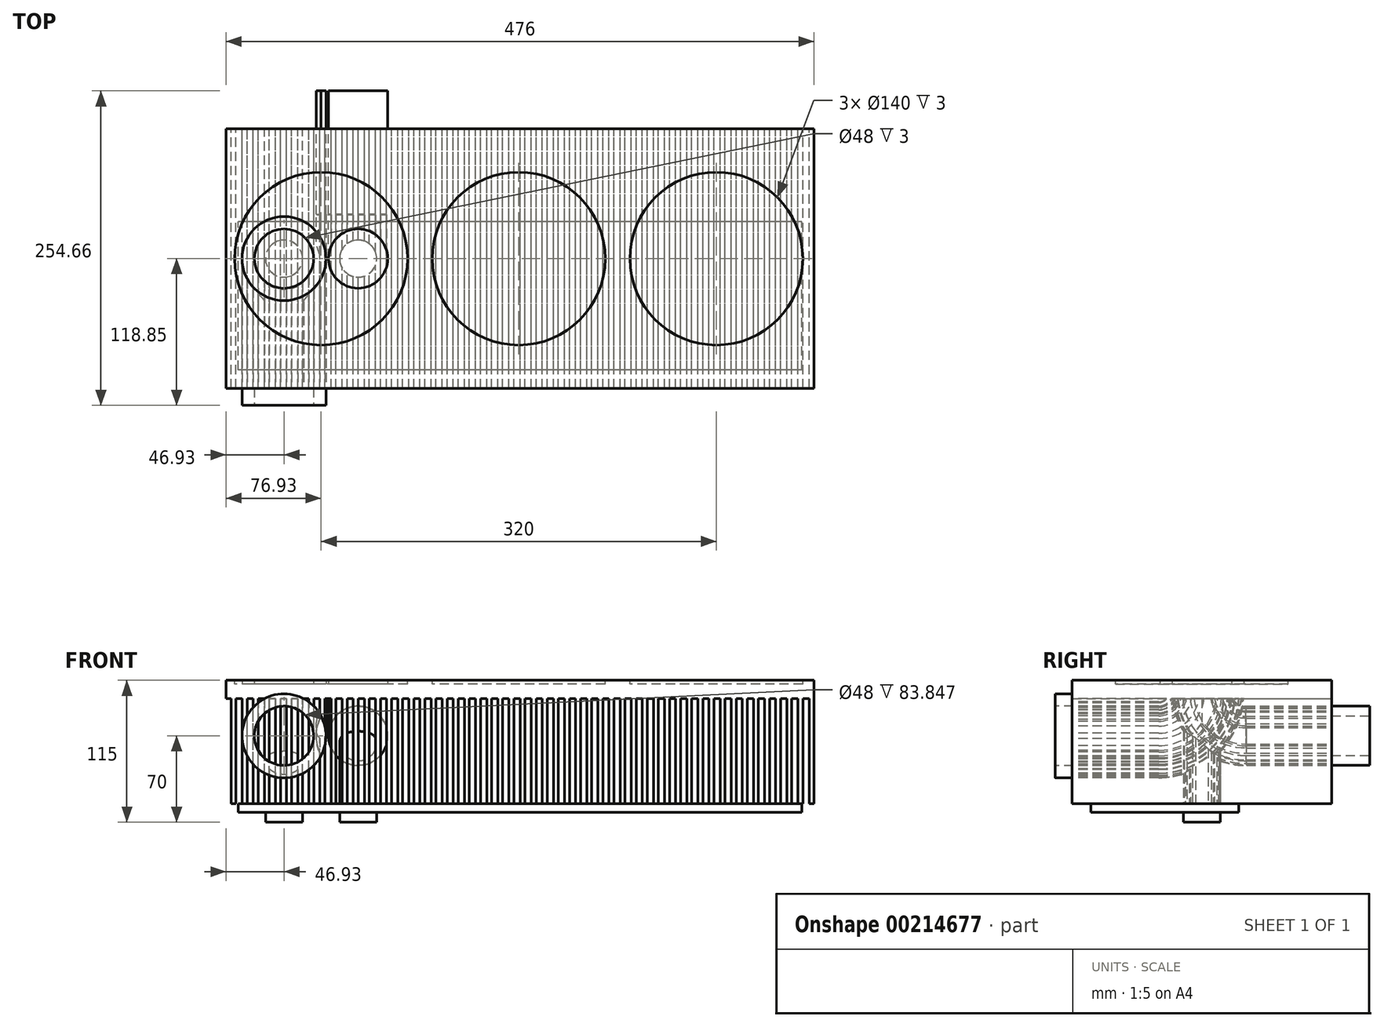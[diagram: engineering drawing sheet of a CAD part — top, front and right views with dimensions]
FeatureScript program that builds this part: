
annotation { "Feature Type Name" : "Feature", "Feature Type Description" : "" }
export const myFeature = defineFeature(function(context is Context, id is Id, definition is map)
    precondition{}
    {
        {
            var Q0;
            Q0=qCreatedBy(makeId("Top.planeOp"),FACE);
            var sketch = newSketch(context, id + "F0", { "sketchPlane" : qUnion([Q0])});
            skLineSegment(sketch, "E0.bottom", {"start": v(-236.93, 105) * mm, "end": v(239.07, 105) * mm});
            skLineSegment(sketch, "E0.top", {"start": v(-236.93, -105) * mm, "end": v(239.07, -105) * mm});
            skLineSegment(sketch, "E0.left", {"start": v(-236.93, 105) * mm, "end": v(-236.93, -105) * mm});
            skLineSegment(sketch, "E0.right", {"start": v(239.07, 105) * mm, "end": v(239.07, -105) * mm});
            skCircle(sketch, "E1", {"center": v(0, 0) * mm, "radius": 70 * mm});
            skCircle(sketch, "E2", {"center": v(160, 0) * mm, "radius": 70 * mm});
            skCircle(sketch, "E3", {"center": v(-160, 0) * mm, "radius": 70 * mm});
            skSolve(sketch);
        }
        {
            var Q0;
            Q0=makeQuery(id+"F0.imprint","IMPRINT",FACE,{"disambiguationData":[TD([[makeQuery(id+"F0.imprint","IMPRINT",EDGE,{"derivedFrom":sQuery(id+"F0.wireOp",EDGE,"E0.bottom")}),-1.0]])]});
            var Q1;
            Q1=makeQuery(id+"F0.imprint","IMPRINT",FACE,{"disambiguationData":[TD([[makeQuery(id+"F0.imprint","IMPRINT",EDGE,{"derivedFrom":sQuery(id+"F0.wireOp",EDGE,"E3")}),1.0]])]});
            var Q2;
            Q2=makeQuery(id+"F0.imprint","IMPRINT",FACE,{"disambiguationData":[TD([[makeQuery(id+"F0.imprint","IMPRINT",EDGE,{"derivedFrom":sQuery(id+"F0.wireOp",EDGE,"E1")}),1.0]])]});
            var Q3;
            Q3=makeQuery(id+"F0.imprint","IMPRINT",FACE,{"disambiguationData":[TD([[makeQuery(id+"F0.imprint","IMPRINT",EDGE,{"derivedFrom":sQuery(id+"F0.wireOp",EDGE,"E2")}),1.0]])]});
            extrude(context, id + "F1", {"entities" : qUnion([Q0, Q1, Q2, Q3]), "oppositeDirection" : true, "depth" : 15 * mm});
        }
        {
            var Q0;
            Q0=makeQuery(id+"F0.imprint","IMPRINT",FACE,{"disambiguationData":[TD([[makeQuery(id+"F0.imprint","IMPRINT",EDGE,{"derivedFrom":sQuery(id+"F0.wireOp",EDGE,"E3")}),1.0]])]});
            var Q1;
            Q1=makeQuery(id+"F0.imprint","IMPRINT",FACE,{"disambiguationData":[TD([[makeQuery(id+"F0.imprint","IMPRINT",EDGE,{"derivedFrom":sQuery(id+"F0.wireOp",EDGE,"E1")}),1.0]])]});
            var Q2;
            Q2=makeQuery(id+"F0.imprint","IMPRINT",FACE,{"disambiguationData":[TD([[makeQuery(id+"F0.imprint","IMPRINT",EDGE,{"derivedFrom":sQuery(id+"F0.wireOp",EDGE,"E2")}),1.0]])]});
            extrude(context, id + "F2", {"entities" : qUnion([Q0, Q1, Q2]), "operationType" : NewBodyOperationType.REMOVE, "oppositeDirection" : true, "depth" : 3 * mm});
        }
        {
            var Q0;
            Q0=makeQuery(id+"F0.imprint","IMPRINT",FACE,{"disambiguationData":[TD([[makeQuery(id+"F0.imprint","IMPRINT",EDGE,{"derivedFrom":sQuery(id+"F0.wireOp",EDGE,"E3")}),1.0]])]});
            var sketch = newSketch(context, id + "F3", { "sketchPlane" : qUnion([Q0])});
            skCircle(sketch, "E4", {"center": v(-190, 0) * mm, "radius": 24 * mm});
            skLineSegment(sketch, "E5", {"start": v(-160, 0) * mm, "end": v(-160, 31.63) * mm});
            skCircle(sketch, "E6.MirrorC", {"center": v(-130, 0) * mm, "radius": 24 * mm});
            skCircle(sketch, "E7", {"center": v(-190, 0) * mm, "radius": 34 * mm});
            skCircle(sketch, "E8.MirrorC", {"center": v(-130, 0) * mm, "radius": 34 * mm});
            skSolve(sketch);
        }
        {
            var Q0;
            Q0=makeQuery(id+"F1.opExtrude","CAP_FACE",FACE,{"disambiguationData":[OSD([sQuery(id+"F0.wireOp",EDGE,"E0.bottom"),sQuery(id+"F0.wireOp",EDGE,"E0.top"),sQuery(id+"F0.wireOp",EDGE,"E0.left"),sQuery(id+"F0.wireOp",EDGE,"E0.right")])],"isStart":false});
            var sketch = newSketch(context, id + "F4", { "sketchPlane" : qUnion([Q0])});
            skLineSegment(sketch, "E9", {"start": v(-130, 0) * mm, "end": v(-130, -36.8) * mm});
            skSolve(sketch);
        }
        {
            var Q0;
            Q0=qCreatedBy(makeId("Right.planeOp"),FACE);
            cPlane(context, id + "F5", {"entities" : qUnion([Q0]), "cplaneType" : CPlaneType.OFFSET, "offset" : 130 * mm, "oppositeDirection" : true, "width" : 150 * mm, "height" : 150 * mm});
        }
        {
            var Q0;
            Q0=qCreatedBy(id+"F5.planeOp",FACE);
            var sketch = newSketch(context, id + "F6", { "sketchPlane" : qUnion([Q0])});
            skLineSegment(sketch, "E10", {"start": v(0, 0) * mm, "end": v(0, -10) * mm});
            skLineSegment(sketch, "E11", {"start": v(0, -10) * mm, "end": v(35, -10) * mm});
            skArc(sketch, "E12", {"start": v(0, -10) * mm, "mid": v(10.54, -35.03) * mm, "end": v(35.8, -45) * mm});
            skLineSegment(sketch, "E13", {"start": v(35.8, -45) * mm, "end": v(135.8, -45) * mm});
            skSolve(sketch);
        }
        {
            var Q0;
            Q0=qCreatedBy(id+"F5.planeOp",FACE);
            cPlane(context, id + "F7", {"entities" : qUnion([Q0]), "cplaneType" : CPlaneType.OFFSET, "offset" : 60 * mm, "oppositeDirection" : true, "width" : 150 * mm, "height" : 150 * mm});
        }
        {
            var Q0;
            Q0=qCreatedBy(id+"F7.planeOp",FACE);
            var sketch = newSketch(context, id + "F8", { "sketchPlane" : qUnion([Q0])});
            skLineSegment(sketch, "E14", {"start": v(0, 0) * mm, "end": v(0, -10) * mm});
            skLineSegment(sketch, "E15", {"start": v(0, -10) * mm, "end": v(-35, -10) * mm});
            skArc(sketch, "E16", {"start": v(-35, -45) * mm, "mid": v(-10.25, -34.75) * mm, "end": v(0, -10) * mm});
            skLineSegment(sketch, "E17", {"start": v(-35, -45) * mm, "end": v(-118.85, -45) * mm});
            skSolve(sketch);
        }
        {
            var Q0;
            {var subQ0=sQuery(id+"F3.wireOp",EDGE,"E8.MirrorC");var subQ1=sQuery(id+"F3.wireOp",EDGE,"E7");var subQ2=makeQuery(id+"F3.imprint","INTERSECT",VERTEX,{"disambiguationData":[OD(0.0)],"derivedFrom":[subQ1,subQ0]});Q0=makeQuery(id+"F3.imprint","IMPRINT",FACE,{"disambiguationData":[TD([[makeQuery(id+"F3.imprint","IMPRINT",EDGE,{"disambiguationData":[TD([[subQ2,-1.0]])],"derivedFrom":subQ1}),1.0]])]});}
            var Q1;
            Q1=makeQuery(id+"F3.imprint","IMPRINT",FACE,{"disambiguationData":[TD([[makeQuery(id+"F3.imprint","IMPRINT",EDGE,{"derivedFrom":sQuery(id+"F3.wireOp",EDGE,"E4")}),-1.0]])]});
            var Q2;
            Q2=sQuery(id+"F8.wireOp",EDGE,"E17");
            var Q3;
            Q3=sQuery(id+"F8.wireOp",EDGE,"E16");
            var Q4;
            Q4=sQuery(id+"F8.wireOp",EDGE,"E14");
            sweep(context, id + "F9", {"operationType" : NewBodyOperationType.ADD, "profiles" : qUnion([Q0, Q1]), "path" : qUnion([Q2, Q3, Q4])});
        }
        {
            var Q0;
            Q0=makeQuery(id+"F4.imprint","IMPRINT",FACE,{"disambiguationData":[TD([[makeQuery(id+"F4.imprint","IMPRINT",EDGE,{"derivedFrom":makeQuery(id+"F1.opExtrude","CAP_EDGE",EDGE,{"disambiguationData":[OSD([sQuery(id+"F0.wireOp",EDGE,"E0.bottom")])],"isStart":false})}),1.0]])]});
            var sketch = newSketch(context, id + "F10", { "sketchPlane" : qUnion([Q0])});
            skLineSegment(sketch, "E18.bottom", {"start": v(235.07, 105) * mm, "end": v(239.07, 105) * mm});
            skLineSegment(sketch, "E18.top", {"start": v(235.07, -105) * mm, "end": v(239.07, -105) * mm});
            skLineSegment(sketch, "E18.left", {"start": v(235.07, 105) * mm, "end": v(235.07, -105) * mm});
            skLineSegment(sketch, "E18.right", {"start": v(239.07, 105) * mm, "end": v(239.07, -105) * mm});
            skLineSegment(sketch, "E19.1.0.0", {"start": v(226.07, 105) * mm, "end": v(226.07, -105) * mm});
            skLineSegment(sketch, "E19.1.0.1", {"start": v(230.07, 105) * mm, "end": v(230.07, -105) * mm});
            skLineSegment(sketch, "E19.1.0.2", {"start": v(226.07, 105) * mm, "end": v(230.07, 105) * mm});
            skLineSegment(sketch, "E19.1.0.3", {"start": v(226.07, -105) * mm, "end": v(230.07, -105) * mm});
            skLineSegment(sketch, "E19.2.0.0", {"start": v(217.07, 105) * mm, "end": v(217.07, -105) * mm});
            skLineSegment(sketch, "E19.2.0.1", {"start": v(221.07, 105) * mm, "end": v(221.07, -105) * mm});
            skLineSegment(sketch, "E19.2.0.2", {"start": v(217.07, 105) * mm, "end": v(221.07, 105) * mm});
            skLineSegment(sketch, "E19.2.0.3", {"start": v(217.07, -105) * mm, "end": v(221.07, -105) * mm});
            skLineSegment(sketch, "E19.3.0.0", {"start": v(208.07, 105) * mm, "end": v(208.07, -105) * mm});
            skLineSegment(sketch, "E19.3.0.1", {"start": v(212.07, 105) * mm, "end": v(212.07, -105) * mm});
            skLineSegment(sketch, "E19.3.0.2", {"start": v(208.07, 105) * mm, "end": v(212.07, 105) * mm});
            skLineSegment(sketch, "E19.3.0.3", {"start": v(208.07, -105) * mm, "end": v(212.07, -105) * mm});
            skLineSegment(sketch, "E19.4.0.0", {"start": v(199.07, 105) * mm, "end": v(199.07, -105) * mm});
            skLineSegment(sketch, "E19.4.0.1", {"start": v(203.07, 105) * mm, "end": v(203.07, -105) * mm});
            skLineSegment(sketch, "E19.4.0.2", {"start": v(199.07, 105) * mm, "end": v(203.07, 105) * mm});
            skLineSegment(sketch, "E19.4.0.3", {"start": v(199.07, -105) * mm, "end": v(203.07, -105) * mm});
            skLineSegment(sketch, "E19.5.0.0", {"start": v(190.07, 105) * mm, "end": v(190.07, -105) * mm});
            skLineSegment(sketch, "E19.5.0.1", {"start": v(194.07, 105) * mm, "end": v(194.07, -105) * mm});
            skLineSegment(sketch, "E19.5.0.2", {"start": v(190.07, 105) * mm, "end": v(194.07, 105) * mm});
            skLineSegment(sketch, "E19.5.0.3", {"start": v(190.07, -105) * mm, "end": v(194.07, -105) * mm});
            skLineSegment(sketch, "E19.6.0.0", {"start": v(181.07, 105) * mm, "end": v(181.07, -105) * mm});
            skLineSegment(sketch, "E19.6.0.1", {"start": v(185.07, 105) * mm, "end": v(185.07, -105) * mm});
            skLineSegment(sketch, "E19.6.0.2", {"start": v(181.07, 105) * mm, "end": v(185.07, 105) * mm});
            skLineSegment(sketch, "E19.6.0.3", {"start": v(181.07, -105) * mm, "end": v(185.07, -105) * mm});
            skLineSegment(sketch, "E19.7.0.0", {"start": v(172.07, 105) * mm, "end": v(172.07, -105) * mm});
            skLineSegment(sketch, "E19.7.0.1", {"start": v(176.07, 105) * mm, "end": v(176.07, -105) * mm});
            skLineSegment(sketch, "E19.7.0.2", {"start": v(172.07, 105) * mm, "end": v(176.07, 105) * mm});
            skLineSegment(sketch, "E19.7.0.3", {"start": v(172.07, -105) * mm, "end": v(176.07, -105) * mm});
            skLineSegment(sketch, "E19.8.0.0", {"start": v(163.07, 105) * mm, "end": v(163.07, -105) * mm});
            skLineSegment(sketch, "E19.8.0.1", {"start": v(167.07, 105) * mm, "end": v(167.07, -105) * mm});
            skLineSegment(sketch, "E19.8.0.2", {"start": v(163.07, 105) * mm, "end": v(167.07, 105) * mm});
            skLineSegment(sketch, "E19.8.0.3", {"start": v(163.07, -105) * mm, "end": v(167.07, -105) * mm});
            skLineSegment(sketch, "E19.9.0.0", {"start": v(154.07, 105) * mm, "end": v(154.07, -105) * mm});
            skLineSegment(sketch, "E19.9.0.1", {"start": v(158.07, 105) * mm, "end": v(158.07, -105) * mm});
            skLineSegment(sketch, "E19.9.0.2", {"start": v(154.07, 105) * mm, "end": v(158.07, 105) * mm});
            skLineSegment(sketch, "E19.9.0.3", {"start": v(154.07, -105) * mm, "end": v(158.07, -105) * mm});
            skLineSegment(sketch, "E19.10.0.0", {"start": v(145.07, 105) * mm, "end": v(145.07, -105) * mm});
            skLineSegment(sketch, "E19.10.0.1", {"start": v(149.07, 105) * mm, "end": v(149.07, -105) * mm});
            skLineSegment(sketch, "E19.10.0.2", {"start": v(145.07, 105) * mm, "end": v(149.07, 105) * mm});
            skLineSegment(sketch, "E19.10.0.3", {"start": v(145.07, -105) * mm, "end": v(149.07, -105) * mm});
            skLineSegment(sketch, "E19.11.0.0", {"start": v(136.07, 105) * mm, "end": v(136.07, -105) * mm});
            skLineSegment(sketch, "E19.11.0.1", {"start": v(140.07, 105) * mm, "end": v(140.07, -105) * mm});
            skLineSegment(sketch, "E19.11.0.2", {"start": v(136.07, 105) * mm, "end": v(140.07, 105) * mm});
            skLineSegment(sketch, "E19.11.0.3", {"start": v(136.07, -105) * mm, "end": v(140.07, -105) * mm});
            skLineSegment(sketch, "E19.12.0.0", {"start": v(127.07, 105) * mm, "end": v(127.07, -105) * mm});
            skLineSegment(sketch, "E19.12.0.1", {"start": v(131.07, 105) * mm, "end": v(131.07, -105) * mm});
            skLineSegment(sketch, "E19.12.0.2", {"start": v(127.07, 105) * mm, "end": v(131.07, 105) * mm});
            skLineSegment(sketch, "E19.12.0.3", {"start": v(127.07, -105) * mm, "end": v(131.07, -105) * mm});
            skLineSegment(sketch, "E19.13.0.0", {"start": v(118.07, 105) * mm, "end": v(118.07, -105) * mm});
            skLineSegment(sketch, "E19.13.0.1", {"start": v(122.07, 105) * mm, "end": v(122.07, -105) * mm});
            skLineSegment(sketch, "E19.13.0.2", {"start": v(118.07, 105) * mm, "end": v(122.07, 105) * mm});
            skLineSegment(sketch, "E19.13.0.3", {"start": v(118.07, -105) * mm, "end": v(122.07, -105) * mm});
            skLineSegment(sketch, "E19.14.0.0", {"start": v(109.07, 105) * mm, "end": v(109.07, -105) * mm});
            skLineSegment(sketch, "E19.14.0.1", {"start": v(113.07, 105) * mm, "end": v(113.07, -105) * mm});
            skLineSegment(sketch, "E19.14.0.2", {"start": v(109.07, 105) * mm, "end": v(113.07, 105) * mm});
            skLineSegment(sketch, "E19.14.0.3", {"start": v(109.07, -105) * mm, "end": v(113.07, -105) * mm});
            skLineSegment(sketch, "E19.15.0.0", {"start": v(100.07, 105) * mm, "end": v(100.07, -105) * mm});
            skLineSegment(sketch, "E19.15.0.1", {"start": v(104.07, 105) * mm, "end": v(104.07, -105) * mm});
            skLineSegment(sketch, "E19.15.0.2", {"start": v(100.07, 105) * mm, "end": v(104.07, 105) * mm});
            skLineSegment(sketch, "E19.15.0.3", {"start": v(100.07, -105) * mm, "end": v(104.07, -105) * mm});
            skLineSegment(sketch, "E19.16.0.0", {"start": v(91.07, 105) * mm, "end": v(91.07, -105) * mm});
            skLineSegment(sketch, "E19.16.0.1", {"start": v(95.07, 105) * mm, "end": v(95.07, -105) * mm});
            skLineSegment(sketch, "E19.16.0.2", {"start": v(91.07, 105) * mm, "end": v(95.07, 105) * mm});
            skLineSegment(sketch, "E19.16.0.3", {"start": v(91.07, -105) * mm, "end": v(95.07, -105) * mm});
            skLineSegment(sketch, "E19.17.0.0", {"start": v(82.07, 105) * mm, "end": v(82.07, -105) * mm});
            skLineSegment(sketch, "E19.17.0.1", {"start": v(86.07, 105) * mm, "end": v(86.07, -105) * mm});
            skLineSegment(sketch, "E19.17.0.2", {"start": v(82.07, 105) * mm, "end": v(86.07, 105) * mm});
            skLineSegment(sketch, "E19.17.0.3", {"start": v(82.07, -105) * mm, "end": v(86.07, -105) * mm});
            skLineSegment(sketch, "E19.18.0.0", {"start": v(73.07, 105) * mm, "end": v(73.07, -105) * mm});
            skLineSegment(sketch, "E19.18.0.1", {"start": v(77.07, 105) * mm, "end": v(77.07, -105) * mm});
            skLineSegment(sketch, "E19.18.0.2", {"start": v(73.07, 105) * mm, "end": v(77.07, 105) * mm});
            skLineSegment(sketch, "E19.18.0.3", {"start": v(73.07, -105) * mm, "end": v(77.07, -105) * mm});
            skLineSegment(sketch, "E19.19.0.0", {"start": v(64.07, 105) * mm, "end": v(64.07, -105) * mm});
            skLineSegment(sketch, "E19.19.0.1", {"start": v(68.07, 105) * mm, "end": v(68.07, -105) * mm});
            skLineSegment(sketch, "E19.19.0.2", {"start": v(64.07, 105) * mm, "end": v(68.07, 105) * mm});
            skLineSegment(sketch, "E19.19.0.3", {"start": v(64.07, -105) * mm, "end": v(68.07, -105) * mm});
            skLineSegment(sketch, "E19.20.0.0", {"start": v(55.07, 105) * mm, "end": v(55.07, -105) * mm});
            skLineSegment(sketch, "E19.20.0.1", {"start": v(59.07, 105) * mm, "end": v(59.07, -105) * mm});
            skLineSegment(sketch, "E19.20.0.2", {"start": v(55.07, 105) * mm, "end": v(59.07, 105) * mm});
            skLineSegment(sketch, "E19.20.0.3", {"start": v(55.07, -105) * mm, "end": v(59.07, -105) * mm});
            skLineSegment(sketch, "E19.21.0.0", {"start": v(46.07, 105) * mm, "end": v(46.07, -105) * mm});
            skLineSegment(sketch, "E19.21.0.1", {"start": v(50.07, 105) * mm, "end": v(50.07, -105) * mm});
            skLineSegment(sketch, "E19.21.0.2", {"start": v(46.07, 105) * mm, "end": v(50.07, 105) * mm});
            skLineSegment(sketch, "E19.21.0.3", {"start": v(46.07, -105) * mm, "end": v(50.07, -105) * mm});
            skLineSegment(sketch, "E19.22.0.0", {"start": v(37.07, 105) * mm, "end": v(37.07, -105) * mm});
            skLineSegment(sketch, "E19.22.0.1", {"start": v(41.07, 105) * mm, "end": v(41.07, -105) * mm});
            skLineSegment(sketch, "E19.22.0.2", {"start": v(37.07, 105) * mm, "end": v(41.07, 105) * mm});
            skLineSegment(sketch, "E19.22.0.3", {"start": v(37.07, -105) * mm, "end": v(41.07, -105) * mm});
            skLineSegment(sketch, "E19.23.0.0", {"start": v(28.07, 105) * mm, "end": v(28.07, -105) * mm});
            skLineSegment(sketch, "E19.23.0.1", {"start": v(32.07, 105) * mm, "end": v(32.07, -105) * mm});
            skLineSegment(sketch, "E19.23.0.2", {"start": v(28.07, 105) * mm, "end": v(32.07, 105) * mm});
            skLineSegment(sketch, "E19.23.0.3", {"start": v(28.07, -105) * mm, "end": v(32.07, -105) * mm});
            skLineSegment(sketch, "E19.24.0.0", {"start": v(19.07, 105) * mm, "end": v(19.07, -105) * mm});
            skLineSegment(sketch, "E19.24.0.1", {"start": v(23.07, 105) * mm, "end": v(23.07, -105) * mm});
            skLineSegment(sketch, "E19.24.0.2", {"start": v(19.07, 105) * mm, "end": v(23.07, 105) * mm});
            skLineSegment(sketch, "E19.24.0.3", {"start": v(19.07, -105) * mm, "end": v(23.07, -105) * mm});
            skLineSegment(sketch, "E19.25.0.0", {"start": v(10.07, 105) * mm, "end": v(10.07, -105) * mm});
            skLineSegment(sketch, "E19.25.0.1", {"start": v(14.07, 105) * mm, "end": v(14.07, -105) * mm});
            skLineSegment(sketch, "E19.25.0.2", {"start": v(10.07, 105) * mm, "end": v(14.07, 105) * mm});
            skLineSegment(sketch, "E19.25.0.3", {"start": v(10.07, -105) * mm, "end": v(14.07, -105) * mm});
            skLineSegment(sketch, "E19.26.0.0", {"start": v(1.07, 105) * mm, "end": v(1.07, -105) * mm});
            skLineSegment(sketch, "E19.26.0.1", {"start": v(5.07, 105) * mm, "end": v(5.07, -105) * mm});
            skLineSegment(sketch, "E19.26.0.2", {"start": v(1.07, 105) * mm, "end": v(5.07, 105) * mm});
            skLineSegment(sketch, "E19.26.0.3", {"start": v(1.07, -105) * mm, "end": v(5.07, -105) * mm});
            skLineSegment(sketch, "E19.27.0.0", {"start": v(-7.93, 105) * mm, "end": v(-7.93, -105) * mm});
            skLineSegment(sketch, "E19.27.0.1", {"start": v(-3.93, 105) * mm, "end": v(-3.93, -105) * mm});
            skLineSegment(sketch, "E19.27.0.2", {"start": v(-7.93, 105) * mm, "end": v(-3.93, 105) * mm});
            skLineSegment(sketch, "E19.27.0.3", {"start": v(-7.93, -105) * mm, "end": v(-3.93, -105) * mm});
            skLineSegment(sketch, "E19.28.0.0", {"start": v(-16.93, 105) * mm, "end": v(-16.93, -105) * mm});
            skLineSegment(sketch, "E19.28.0.1", {"start": v(-12.93, 105) * mm, "end": v(-12.93, -105) * mm});
            skLineSegment(sketch, "E19.28.0.2", {"start": v(-16.93, 105) * mm, "end": v(-12.93, 105) * mm});
            skLineSegment(sketch, "E19.28.0.3", {"start": v(-16.93, -105) * mm, "end": v(-12.93, -105) * mm});
            skLineSegment(sketch, "E19.29.0.0", {"start": v(-25.93, 105) * mm, "end": v(-25.93, -105) * mm});
            skLineSegment(sketch, "E19.29.0.1", {"start": v(-21.93, 105) * mm, "end": v(-21.93, -105) * mm});
            skLineSegment(sketch, "E19.29.0.2", {"start": v(-25.93, 105) * mm, "end": v(-21.93, 105) * mm});
            skLineSegment(sketch, "E19.29.0.3", {"start": v(-25.93, -105) * mm, "end": v(-21.93, -105) * mm});
            skLineSegment(sketch, "E19.30.0.0", {"start": v(-34.93, 105) * mm, "end": v(-34.93, -105) * mm});
            skLineSegment(sketch, "E19.30.0.1", {"start": v(-30.93, 105) * mm, "end": v(-30.93, -105) * mm});
            skLineSegment(sketch, "E19.30.0.2", {"start": v(-34.93, 105) * mm, "end": v(-30.93, 105) * mm});
            skLineSegment(sketch, "E19.30.0.3", {"start": v(-34.93, -105) * mm, "end": v(-30.93, -105) * mm});
            skLineSegment(sketch, "E19.31.0.0", {"start": v(-43.93, 105) * mm, "end": v(-43.93, -105) * mm});
            skLineSegment(sketch, "E19.31.0.1", {"start": v(-39.93, 105) * mm, "end": v(-39.93, -105) * mm});
            skLineSegment(sketch, "E19.31.0.2", {"start": v(-43.93, 105) * mm, "end": v(-39.93, 105) * mm});
            skLineSegment(sketch, "E19.31.0.3", {"start": v(-43.93, -105) * mm, "end": v(-39.93, -105) * mm});
            skLineSegment(sketch, "E19.32.0.0", {"start": v(-52.93, 105) * mm, "end": v(-52.93, -105) * mm});
            skLineSegment(sketch, "E19.32.0.1", {"start": v(-48.93, 105) * mm, "end": v(-48.93, -105) * mm});
            skLineSegment(sketch, "E19.32.0.2", {"start": v(-52.93, 105) * mm, "end": v(-48.93, 105) * mm});
            skLineSegment(sketch, "E19.32.0.3", {"start": v(-52.93, -105) * mm, "end": v(-48.93, -105) * mm});
            skLineSegment(sketch, "E19.33.0.0", {"start": v(-61.93, 105) * mm, "end": v(-61.93, -105) * mm});
            skLineSegment(sketch, "E19.33.0.1", {"start": v(-57.93, 105) * mm, "end": v(-57.93, -105) * mm});
            skLineSegment(sketch, "E19.33.0.2", {"start": v(-61.93, 105) * mm, "end": v(-57.93, 105) * mm});
            skLineSegment(sketch, "E19.33.0.3", {"start": v(-61.93, -105) * mm, "end": v(-57.93, -105) * mm});
            skLineSegment(sketch, "E19.34.0.0", {"start": v(-70.93, 105) * mm, "end": v(-70.93, -105) * mm});
            skLineSegment(sketch, "E19.34.0.1", {"start": v(-66.93, 105) * mm, "end": v(-66.93, -105) * mm});
            skLineSegment(sketch, "E19.34.0.2", {"start": v(-70.93, 105) * mm, "end": v(-66.93, 105) * mm});
            skLineSegment(sketch, "E19.34.0.3", {"start": v(-70.93, -105) * mm, "end": v(-66.93, -105) * mm});
            skLineSegment(sketch, "E19.35.0.0", {"start": v(-79.93, 105) * mm, "end": v(-79.93, -105) * mm});
            skLineSegment(sketch, "E19.35.0.1", {"start": v(-75.93, 105) * mm, "end": v(-75.93, -105) * mm});
            skLineSegment(sketch, "E19.35.0.2", {"start": v(-79.93, 105) * mm, "end": v(-75.93, 105) * mm});
            skLineSegment(sketch, "E19.35.0.3", {"start": v(-79.93, -105) * mm, "end": v(-75.93, -105) * mm});
            skLineSegment(sketch, "E19.36.0.0", {"start": v(-88.93, 105) * mm, "end": v(-88.93, -105) * mm});
            skLineSegment(sketch, "E19.36.0.1", {"start": v(-84.93, 105) * mm, "end": v(-84.93, -105) * mm});
            skLineSegment(sketch, "E19.36.0.2", {"start": v(-88.93, 105) * mm, "end": v(-84.93, 105) * mm});
            skLineSegment(sketch, "E19.36.0.3", {"start": v(-88.93, -105) * mm, "end": v(-84.93, -105) * mm});
            skLineSegment(sketch, "E19.37.0.0", {"start": v(-97.93, 105) * mm, "end": v(-97.93, -105) * mm});
            skLineSegment(sketch, "E19.37.0.1", {"start": v(-93.93, 105) * mm, "end": v(-93.93, -105) * mm});
            skLineSegment(sketch, "E19.37.0.2", {"start": v(-97.93, 105) * mm, "end": v(-93.93, 105) * mm});
            skLineSegment(sketch, "E19.37.0.3", {"start": v(-97.93, -105) * mm, "end": v(-93.93, -105) * mm});
            skLineSegment(sketch, "E19.38.0.0", {"start": v(-106.93, 105) * mm, "end": v(-106.93, -105) * mm});
            skLineSegment(sketch, "E19.38.0.1", {"start": v(-102.93, 105) * mm, "end": v(-102.93, -105) * mm});
            skLineSegment(sketch, "E19.38.0.2", {"start": v(-106.93, 105) * mm, "end": v(-102.93, 105) * mm});
            skLineSegment(sketch, "E19.38.0.3", {"start": v(-106.93, -105) * mm, "end": v(-102.93, -105) * mm});
            skLineSegment(sketch, "E19.39.0.0", {"start": v(-115.93, 105) * mm, "end": v(-115.93, -105) * mm});
            skLineSegment(sketch, "E19.39.0.1", {"start": v(-111.93, 105) * mm, "end": v(-111.93, -105) * mm});
            skLineSegment(sketch, "E19.39.0.2", {"start": v(-115.93, 105) * mm, "end": v(-111.93, 105) * mm});
            skLineSegment(sketch, "E19.39.0.3", {"start": v(-115.93, -105) * mm, "end": v(-111.93, -105) * mm});
            skLineSegment(sketch, "E19.40.0.0", {"start": v(-124.93, 105) * mm, "end": v(-124.93, -105) * mm});
            skLineSegment(sketch, "E19.40.0.1", {"start": v(-120.93, 105) * mm, "end": v(-120.93, -105) * mm});
            skLineSegment(sketch, "E19.40.0.2", {"start": v(-124.93, 105) * mm, "end": v(-120.93, 105) * mm});
            skLineSegment(sketch, "E19.40.0.3", {"start": v(-124.93, -105) * mm, "end": v(-120.93, -105) * mm});
            skLineSegment(sketch, "E19.41.0.0", {"start": v(-133.93, 105) * mm, "end": v(-133.93, -105) * mm});
            skLineSegment(sketch, "E19.41.0.1", {"start": v(-129.93, 105) * mm, "end": v(-129.93, -105) * mm});
            skLineSegment(sketch, "E19.41.0.2", {"start": v(-133.93, 105) * mm, "end": v(-129.93, 105) * mm});
            skLineSegment(sketch, "E19.41.0.3", {"start": v(-133.93, -105) * mm, "end": v(-129.93, -105) * mm});
            skLineSegment(sketch, "E19.42.0.0", {"start": v(-142.93, 105) * mm, "end": v(-142.93, -105) * mm});
            skLineSegment(sketch, "E19.42.0.1", {"start": v(-138.93, 105) * mm, "end": v(-138.93, -105) * mm});
            skLineSegment(sketch, "E19.42.0.2", {"start": v(-142.93, 105) * mm, "end": v(-138.93, 105) * mm});
            skLineSegment(sketch, "E19.42.0.3", {"start": v(-142.93, -105) * mm, "end": v(-138.93, -105) * mm});
            skLineSegment(sketch, "E19.43.0.0", {"start": v(-151.93, 105) * mm, "end": v(-151.93, -105) * mm});
            skLineSegment(sketch, "E19.43.0.1", {"start": v(-147.93, 105) * mm, "end": v(-147.93, -105) * mm});
            skLineSegment(sketch, "E19.43.0.2", {"start": v(-151.93, 105) * mm, "end": v(-147.93, 105) * mm});
            skLineSegment(sketch, "E19.43.0.3", {"start": v(-151.93, -105) * mm, "end": v(-147.93, -105) * mm});
            skLineSegment(sketch, "E19.44.0.0", {"start": v(-160.93, 105) * mm, "end": v(-160.93, -105) * mm});
            skLineSegment(sketch, "E19.44.0.1", {"start": v(-156.93, 105) * mm, "end": v(-156.93, -105) * mm});
            skLineSegment(sketch, "E19.44.0.2", {"start": v(-160.93, 105) * mm, "end": v(-156.93, 105) * mm});
            skLineSegment(sketch, "E19.44.0.3", {"start": v(-160.93, -105) * mm, "end": v(-156.93, -105) * mm});
            skLineSegment(sketch, "E19.45.0.0", {"start": v(-169.93, 105) * mm, "end": v(-169.93, -105) * mm});
            skLineSegment(sketch, "E19.45.0.1", {"start": v(-165.93, 105) * mm, "end": v(-165.93, -105) * mm});
            skLineSegment(sketch, "E19.45.0.2", {"start": v(-169.93, 105) * mm, "end": v(-165.93, 105) * mm});
            skLineSegment(sketch, "E19.45.0.3", {"start": v(-169.93, -105) * mm, "end": v(-165.93, -105) * mm});
            skLineSegment(sketch, "E19.46.0.0", {"start": v(-178.93, 105) * mm, "end": v(-178.93, -105) * mm});
            skLineSegment(sketch, "E19.46.0.1", {"start": v(-174.93, 105) * mm, "end": v(-174.93, -105) * mm});
            skLineSegment(sketch, "E19.46.0.2", {"start": v(-178.93, 105) * mm, "end": v(-174.93, 105) * mm});
            skLineSegment(sketch, "E19.46.0.3", {"start": v(-178.93, -105) * mm, "end": v(-174.93, -105) * mm});
            skLineSegment(sketch, "E19.47.0.0", {"start": v(-187.93, 105) * mm, "end": v(-187.93, -105) * mm});
            skLineSegment(sketch, "E19.47.0.1", {"start": v(-183.93, 105) * mm, "end": v(-183.93, -105) * mm});
            skLineSegment(sketch, "E19.47.0.2", {"start": v(-187.93, 105) * mm, "end": v(-183.93, 105) * mm});
            skLineSegment(sketch, "E19.47.0.3", {"start": v(-187.93, -105) * mm, "end": v(-183.93, -105) * mm});
            skLineSegment(sketch, "E19.48.0.0", {"start": v(-196.93, 105) * mm, "end": v(-196.93, -105) * mm});
            skLineSegment(sketch, "E19.48.0.1", {"start": v(-192.93, 105) * mm, "end": v(-192.93, -105) * mm});
            skLineSegment(sketch, "E19.48.0.2", {"start": v(-196.93, 105) * mm, "end": v(-192.93, 105) * mm});
            skLineSegment(sketch, "E19.48.0.3", {"start": v(-196.93, -105) * mm, "end": v(-192.93, -105) * mm});
            skLineSegment(sketch, "E19.49.0.0", {"start": v(-205.93, 105) * mm, "end": v(-205.93, -105) * mm});
            skLineSegment(sketch, "E19.49.0.1", {"start": v(-201.93, 105) * mm, "end": v(-201.93, -105) * mm});
            skLineSegment(sketch, "E19.49.0.2", {"start": v(-205.93, 105) * mm, "end": v(-201.93, 105) * mm});
            skLineSegment(sketch, "E19.49.0.3", {"start": v(-205.93, -105) * mm, "end": v(-201.93, -105) * mm});
            skLineSegment(sketch, "E19.direction1", {"start": v(235.07, -105) * mm, "end": v(226.07, -105) * mm, "construction": true});
            skLineSegment(sketch, "E20.0.50.0", {"start": v(-214.93, 105) * mm, "end": v(-214.93, -105) * mm});
            skLineSegment(sketch, "E20.3.50.0", {"start": v(-210.93, 105) * mm, "end": v(-210.93, -105) * mm});
            skLineSegment(sketch, "E20.6.50.0", {"start": v(-214.93, 105) * mm, "end": v(-210.93, 105) * mm});
            skLineSegment(sketch, "E20.9.50.0", {"start": v(-214.93, -105) * mm, "end": v(-210.93, -105) * mm});
            skLineSegment(sketch, "E20.0.51.0", {"start": v(-223.93, 105) * mm, "end": v(-223.93, -105) * mm});
            skLineSegment(sketch, "E20.3.51.0", {"start": v(-219.93, 105) * mm, "end": v(-219.93, -105) * mm});
            skLineSegment(sketch, "E20.6.51.0", {"start": v(-223.93, 105) * mm, "end": v(-219.93, 105) * mm});
            skLineSegment(sketch, "E20.9.51.0", {"start": v(-223.93, -105) * mm, "end": v(-219.93, -105) * mm});
            skLineSegment(sketch, "E20.0.52.0", {"start": v(-232.93, 105) * mm, "end": v(-232.93, -105) * mm});
            skLineSegment(sketch, "E20.3.52.0", {"start": v(-228.93, 105) * mm, "end": v(-228.93, -105) * mm});
            skLineSegment(sketch, "E20.6.52.0", {"start": v(-232.93, 105) * mm, "end": v(-228.93, 105) * mm});
            skLineSegment(sketch, "E20.9.52.0", {"start": v(-232.93, -105) * mm, "end": v(-228.93, -105) * mm});
            skSolve(sketch);
        }
        {
            var Q0;
            Q0=makeQuery(id+"F10.imprint","IMPRINT",FACE,{"disambiguationData":[TD([[makeQuery(id+"F10.imprint","IMPRINT",EDGE,{"derivedFrom":sQuery(id+"F10.wireOp",EDGE,"E18.bottom")}),-1.0]])]});
            var Q1;
            Q1=makeQuery(id+"F10.imprint","IMPRINT",FACE,{"disambiguationData":[TD([[makeQuery(id+"F10.imprint","IMPRINT",EDGE,{"derivedFrom":sQuery(id+"F10.wireOp",EDGE,"E19.1.0.0")}),1.0]])]});
            var Q2;
            Q2=makeQuery(id+"F10.imprint","IMPRINT",FACE,{"disambiguationData":[TD([[makeQuery(id+"F10.imprint","IMPRINT",EDGE,{"derivedFrom":sQuery(id+"F10.wireOp",EDGE,"E19.2.0.0")}),1.0]])]});
            var Q3;
            Q3=makeQuery(id+"F10.imprint","IMPRINT",FACE,{"disambiguationData":[TD([[makeQuery(id+"F10.imprint","IMPRINT",EDGE,{"derivedFrom":sQuery(id+"F10.wireOp",EDGE,"E19.3.0.0")}),1.0]])]});
            var Q4;
            Q4=makeQuery(id+"F10.imprint","IMPRINT",FACE,{"disambiguationData":[TD([[makeQuery(id+"F10.imprint","IMPRINT",EDGE,{"derivedFrom":sQuery(id+"F10.wireOp",EDGE,"E19.4.0.0")}),1.0]])]});
            var Q5;
            Q5=makeQuery(id+"F10.imprint","IMPRINT",FACE,{"disambiguationData":[TD([[makeQuery(id+"F10.imprint","IMPRINT",EDGE,{"derivedFrom":sQuery(id+"F10.wireOp",EDGE,"E19.5.0.0")}),1.0]])]});
            var Q6;
            Q6=makeQuery(id+"F10.imprint","IMPRINT",FACE,{"disambiguationData":[TD([[makeQuery(id+"F10.imprint","IMPRINT",EDGE,{"derivedFrom":sQuery(id+"F10.wireOp",EDGE,"E19.7.0.0")}),1.0]])]});
            var Q7;
            Q7=makeQuery(id+"F10.imprint","IMPRINT",FACE,{"disambiguationData":[TD([[makeQuery(id+"F10.imprint","IMPRINT",EDGE,{"derivedFrom":sQuery(id+"F10.wireOp",EDGE,"E19.6.0.0")}),1.0]])]});
            var Q8;
            Q8=makeQuery(id+"F10.imprint","IMPRINT",FACE,{"disambiguationData":[TD([[makeQuery(id+"F10.imprint","IMPRINT",EDGE,{"derivedFrom":sQuery(id+"F10.wireOp",EDGE,"E19.8.0.0")}),1.0]])]});
            var Q9;
            Q9=makeQuery(id+"F10.imprint","IMPRINT",FACE,{"disambiguationData":[TD([[makeQuery(id+"F10.imprint","IMPRINT",EDGE,{"derivedFrom":sQuery(id+"F10.wireOp",EDGE,"E19.9.0.0")}),1.0]])]});
            var Q10;
            Q10=makeQuery(id+"F10.imprint","IMPRINT",FACE,{"disambiguationData":[TD([[makeQuery(id+"F10.imprint","IMPRINT",EDGE,{"derivedFrom":sQuery(id+"F10.wireOp",EDGE,"E19.10.0.0")}),1.0]])]});
            var Q11;
            Q11=makeQuery(id+"F10.imprint","IMPRINT",FACE,{"disambiguationData":[TD([[makeQuery(id+"F10.imprint","IMPRINT",EDGE,{"derivedFrom":sQuery(id+"F10.wireOp",EDGE,"E19.11.0.0")}),1.0]])]});
            var Q12;
            Q12=makeQuery(id+"F10.imprint","IMPRINT",FACE,{"disambiguationData":[TD([[makeQuery(id+"F10.imprint","IMPRINT",EDGE,{"derivedFrom":sQuery(id+"F10.wireOp",EDGE,"E19.12.0.0")}),1.0]])]});
            var Q13;
            Q13=makeQuery(id+"F10.imprint","IMPRINT",FACE,{"disambiguationData":[TD([[makeQuery(id+"F10.imprint","IMPRINT",EDGE,{"derivedFrom":sQuery(id+"F10.wireOp",EDGE,"E19.13.0.0")}),1.0]])]});
            var Q14;
            Q14=makeQuery(id+"F10.imprint","IMPRINT",FACE,{"disambiguationData":[TD([[makeQuery(id+"F10.imprint","IMPRINT",EDGE,{"derivedFrom":sQuery(id+"F10.wireOp",EDGE,"E19.14.0.0")}),1.0]])]});
            var Q15;
            Q15=makeQuery(id+"F10.imprint","IMPRINT",FACE,{"disambiguationData":[TD([[makeQuery(id+"F10.imprint","IMPRINT",EDGE,{"derivedFrom":sQuery(id+"F10.wireOp",EDGE,"E19.15.0.0")}),1.0]])]});
            var Q16;
            Q16=makeQuery(id+"F10.imprint","IMPRINT",FACE,{"disambiguationData":[TD([[makeQuery(id+"F10.imprint","IMPRINT",EDGE,{"derivedFrom":sQuery(id+"F10.wireOp",EDGE,"E19.16.0.0")}),1.0]])]});
            var Q17;
            Q17=makeQuery(id+"F10.imprint","IMPRINT",FACE,{"disambiguationData":[TD([[makeQuery(id+"F10.imprint","IMPRINT",EDGE,{"derivedFrom":sQuery(id+"F10.wireOp",EDGE,"E19.17.0.0")}),1.0]])]});
            var Q18;
            Q18=makeQuery(id+"F10.imprint","IMPRINT",FACE,{"disambiguationData":[TD([[makeQuery(id+"F10.imprint","IMPRINT",EDGE,{"derivedFrom":sQuery(id+"F10.wireOp",EDGE,"E19.18.0.0")}),1.0]])]});
            var Q19;
            Q19=makeQuery(id+"F10.imprint","IMPRINT",FACE,{"disambiguationData":[TD([[makeQuery(id+"F10.imprint","IMPRINT",EDGE,{"derivedFrom":sQuery(id+"F10.wireOp",EDGE,"E19.19.0.0")}),1.0]])]});
            var Q20;
            Q20=makeQuery(id+"F10.imprint","IMPRINT",FACE,{"disambiguationData":[TD([[makeQuery(id+"F10.imprint","IMPRINT",EDGE,{"derivedFrom":sQuery(id+"F10.wireOp",EDGE,"E19.20.0.0")}),1.0]])]});
            var Q21;
            Q21=makeQuery(id+"F10.imprint","IMPRINT",FACE,{"disambiguationData":[TD([[makeQuery(id+"F10.imprint","IMPRINT",EDGE,{"derivedFrom":sQuery(id+"F10.wireOp",EDGE,"E19.21.0.0")}),1.0]])]});
            var Q22;
            Q22=makeQuery(id+"F10.imprint","IMPRINT",FACE,{"disambiguationData":[TD([[makeQuery(id+"F10.imprint","IMPRINT",EDGE,{"derivedFrom":sQuery(id+"F10.wireOp",EDGE,"E19.22.0.0")}),1.0]])]});
            var Q23;
            Q23=makeQuery(id+"F10.imprint","IMPRINT",FACE,{"disambiguationData":[TD([[makeQuery(id+"F10.imprint","IMPRINT",EDGE,{"derivedFrom":sQuery(id+"F10.wireOp",EDGE,"E19.23.0.0")}),1.0]])]});
            var Q24;
            Q24=makeQuery(id+"F10.imprint","IMPRINT",FACE,{"disambiguationData":[TD([[makeQuery(id+"F10.imprint","IMPRINT",EDGE,{"derivedFrom":sQuery(id+"F10.wireOp",EDGE,"E19.24.0.0")}),1.0]])]});
            var Q25;
            Q25=makeQuery(id+"F10.imprint","IMPRINT",FACE,{"disambiguationData":[TD([[makeQuery(id+"F10.imprint","IMPRINT",EDGE,{"derivedFrom":sQuery(id+"F10.wireOp",EDGE,"E19.25.0.0")}),1.0]])]});
            var Q26;
            Q26=makeQuery(id+"F10.imprint","IMPRINT",FACE,{"disambiguationData":[TD([[makeQuery(id+"F10.imprint","IMPRINT",EDGE,{"derivedFrom":sQuery(id+"F10.wireOp",EDGE,"E19.26.0.0")}),1.0]])]});
            var Q27;
            Q27=makeQuery(id+"F10.imprint","IMPRINT",FACE,{"disambiguationData":[TD([[makeQuery(id+"F10.imprint","IMPRINT",EDGE,{"derivedFrom":sQuery(id+"F10.wireOp",EDGE,"E19.27.0.0")}),1.0]])]});
            var Q28;
            Q28=makeQuery(id+"F10.imprint","IMPRINT",FACE,{"disambiguationData":[TD([[makeQuery(id+"F10.imprint","IMPRINT",EDGE,{"derivedFrom":sQuery(id+"F10.wireOp",EDGE,"E19.28.0.0")}),1.0]])]});
            var Q29;
            Q29=makeQuery(id+"F10.imprint","IMPRINT",FACE,{"disambiguationData":[TD([[makeQuery(id+"F10.imprint","IMPRINT",EDGE,{"derivedFrom":sQuery(id+"F10.wireOp",EDGE,"E19.29.0.0")}),1.0]])]});
            var Q30;
            Q30=makeQuery(id+"F10.imprint","IMPRINT",FACE,{"disambiguationData":[TD([[makeQuery(id+"F10.imprint","IMPRINT",EDGE,{"derivedFrom":sQuery(id+"F10.wireOp",EDGE,"E19.31.0.0")}),1.0]])]});
            var Q31;
            Q31=makeQuery(id+"F10.imprint","IMPRINT",FACE,{"disambiguationData":[TD([[makeQuery(id+"F10.imprint","IMPRINT",EDGE,{"derivedFrom":sQuery(id+"F10.wireOp",EDGE,"E19.30.0.0")}),1.0]])]});
            var Q32;
            Q32=makeQuery(id+"F10.imprint","IMPRINT",FACE,{"disambiguationData":[TD([[makeQuery(id+"F10.imprint","IMPRINT",EDGE,{"derivedFrom":sQuery(id+"F10.wireOp",EDGE,"E19.32.0.0")}),1.0]])]});
            var Q33;
            Q33=makeQuery(id+"F10.imprint","IMPRINT",FACE,{"disambiguationData":[TD([[makeQuery(id+"F10.imprint","IMPRINT",EDGE,{"derivedFrom":sQuery(id+"F10.wireOp",EDGE,"E19.33.0.0")}),1.0]])]});
            var Q34;
            Q34=makeQuery(id+"F10.imprint","IMPRINT",FACE,{"disambiguationData":[TD([[makeQuery(id+"F10.imprint","IMPRINT",EDGE,{"derivedFrom":sQuery(id+"F10.wireOp",EDGE,"E19.34.0.0")}),1.0]])]});
            var Q35;
            Q35=makeQuery(id+"F10.imprint","IMPRINT",FACE,{"disambiguationData":[TD([[makeQuery(id+"F10.imprint","IMPRINT",EDGE,{"derivedFrom":sQuery(id+"F10.wireOp",EDGE,"E19.35.0.0")}),1.0]])]});
            var Q36;
            Q36=makeQuery(id+"F10.imprint","IMPRINT",FACE,{"disambiguationData":[TD([[makeQuery(id+"F10.imprint","IMPRINT",EDGE,{"derivedFrom":sQuery(id+"F10.wireOp",EDGE,"E19.36.0.0")}),1.0]])]});
            var Q37;
            Q37=makeQuery(id+"F10.imprint","IMPRINT",FACE,{"disambiguationData":[TD([[makeQuery(id+"F10.imprint","IMPRINT",EDGE,{"derivedFrom":sQuery(id+"F10.wireOp",EDGE,"E19.37.0.0")}),1.0]])]});
            var Q38;
            Q38=makeQuery(id+"F10.imprint","IMPRINT",FACE,{"disambiguationData":[TD([[makeQuery(id+"F10.imprint","IMPRINT",EDGE,{"derivedFrom":sQuery(id+"F10.wireOp",EDGE,"E19.38.0.0")}),1.0]])]});
            var Q39;
            Q39=makeQuery(id+"F10.imprint","IMPRINT",FACE,{"disambiguationData":[TD([[makeQuery(id+"F10.imprint","IMPRINT",EDGE,{"derivedFrom":sQuery(id+"F10.wireOp",EDGE,"E19.39.0.0")}),1.0]])]});
            var Q40;
            Q40=makeQuery(id+"F10.imprint","IMPRINT",FACE,{"disambiguationData":[TD([[makeQuery(id+"F10.imprint","IMPRINT",EDGE,{"derivedFrom":sQuery(id+"F10.wireOp",EDGE,"E19.40.0.0")}),1.0]])]});
            var Q41;
            Q41=makeQuery(id+"F10.imprint","IMPRINT",FACE,{"disambiguationData":[TD([[makeQuery(id+"F10.imprint","IMPRINT",EDGE,{"derivedFrom":sQuery(id+"F10.wireOp",EDGE,"E19.41.0.0")}),1.0]])]});
            var Q42;
            Q42=makeQuery(id+"F10.imprint","IMPRINT",FACE,{"disambiguationData":[TD([[makeQuery(id+"F10.imprint","IMPRINT",EDGE,{"derivedFrom":sQuery(id+"F10.wireOp",EDGE,"E19.42.0.0")}),1.0]])]});
            var Q43;
            Q43=makeQuery(id+"F10.imprint","IMPRINT",FACE,{"disambiguationData":[TD([[makeQuery(id+"F10.imprint","IMPRINT",EDGE,{"derivedFrom":sQuery(id+"F10.wireOp",EDGE,"E19.43.0.0")}),1.0]])]});
            var Q44;
            Q44=makeQuery(id+"F10.imprint","IMPRINT",FACE,{"disambiguationData":[TD([[makeQuery(id+"F10.imprint","IMPRINT",EDGE,{"derivedFrom":sQuery(id+"F10.wireOp",EDGE,"E19.44.0.0")}),1.0]])]});
            var Q45;
            Q45=makeQuery(id+"F10.imprint","IMPRINT",FACE,{"disambiguationData":[TD([[makeQuery(id+"F10.imprint","IMPRINT",EDGE,{"derivedFrom":sQuery(id+"F10.wireOp",EDGE,"E19.45.0.0")}),1.0]])]});
            var Q46;
            Q46=makeQuery(id+"F10.imprint","IMPRINT",FACE,{"disambiguationData":[TD([[makeQuery(id+"F10.imprint","IMPRINT",EDGE,{"derivedFrom":sQuery(id+"F10.wireOp",EDGE,"E19.46.0.0")}),1.0]])]});
            var Q47;
            Q47=makeQuery(id+"F10.imprint","IMPRINT",FACE,{"disambiguationData":[TD([[makeQuery(id+"F10.imprint","IMPRINT",EDGE,{"derivedFrom":sQuery(id+"F10.wireOp",EDGE,"E19.47.0.0")}),1.0]])]});
            var Q48;
            Q48=makeQuery(id+"F10.imprint","IMPRINT",FACE,{"disambiguationData":[TD([[makeQuery(id+"F10.imprint","IMPRINT",EDGE,{"derivedFrom":sQuery(id+"F10.wireOp",EDGE,"E19.48.0.0")}),1.0]])]});
            var Q49;
            Q49=makeQuery(id+"F10.imprint","IMPRINT",FACE,{"disambiguationData":[TD([[makeQuery(id+"F10.imprint","IMPRINT",EDGE,{"derivedFrom":sQuery(id+"F10.wireOp",EDGE,"E19.49.0.0")}),1.0]])]});
            var Q50;
            Q50=makeQuery(id+"F10.imprint","IMPRINT",FACE,{"disambiguationData":[TD([[makeQuery(id+"F10.imprint","IMPRINT",EDGE,{"derivedFrom":sQuery(id+"F10.wireOp",EDGE,"E20.0.50.0")}),1.0]])]});
            var Q51;
            Q51=makeQuery(id+"F10.imprint","IMPRINT",FACE,{"disambiguationData":[TD([[makeQuery(id+"F10.imprint","IMPRINT",EDGE,{"derivedFrom":sQuery(id+"F10.wireOp",EDGE,"E20.0.51.0")}),1.0]])]});
            var Q52;
            Q52=makeQuery(id+"F10.imprint","IMPRINT",FACE,{"disambiguationData":[TD([[makeQuery(id+"F10.imprint","IMPRINT",EDGE,{"derivedFrom":sQuery(id+"F10.wireOp",EDGE,"E20.0.52.0")}),1.0]])]});
            extrude(context, id + "F11", {"entities" : qUnion([Q0, Q1, Q2, Q3, Q4, Q5, Q6, Q7, Q8, Q9, Q10, Q11, Q12, Q13, Q14, Q15, Q16, Q17, Q18, Q19, Q20, Q21, Q22, Q23, Q24, Q25, Q26, Q27, Q28, Q29, Q30, Q31, Q32, Q33, Q34, Q35, Q36, Q37, Q38, Q39, Q40, Q41, Q42, Q43, Q44, Q45, Q46, Q47, Q48, Q49, Q50, Q51, Q52]), "operationType" : NewBodyOperationType.ADD, "depth" : 85 * mm});
        }
        {
            var Q0;
            Q0=makeQuery(id+"F3.imprint","IMPRINT",FACE,{"disambiguationData":[TD([[makeQuery(id+"F3.imprint","IMPRINT",EDGE,{"derivedFrom":sQuery(id+"F3.wireOp",EDGE,"E6.MirrorC")}),1.0]])]});
            var Q1;
            {var subQ0=sQuery(id+"F3.wireOp",EDGE,"E8.MirrorC");var subQ1=sQuery(id+"F3.wireOp",EDGE,"E7");var subQ2=makeQuery(id+"F3.imprint","INTERSECT",VERTEX,{"disambiguationData":[OD(0.0)],"derivedFrom":[subQ1,subQ0]});Q1=makeQuery(id+"F3.imprint","IMPRINT",FACE,{"disambiguationData":[TD([[makeQuery(id+"F3.imprint","IMPRINT",EDGE,{"disambiguationData":[TD([[subQ2,-1.0]])],"derivedFrom":subQ1}),1.0]])]});}
            var Q2;
            Q2=sQuery(id+"F6.wireOp",EDGE,"E10");
            var Q3;
            Q3=sQuery(id+"F6.wireOp",EDGE,"E12");
            var Q4;
            Q4=sQuery(id+"F6.wireOp",EDGE,"E13");
            sweep(context, id + "F12", {"operationType" : NewBodyOperationType.ADD, "profiles" : qUnion([Q0, Q1]), "path" : qUnion([Q2, Q3, Q4])});
        }
        {
            var Q0;
            Q0=makeQuery(id+"F4.imprint","IMPRINT",FACE,{"disambiguationData":[TD([[makeQuery(id+"F4.imprint","IMPRINT",EDGE,{"derivedFrom":makeQuery(id+"F1.opExtrude","CAP_EDGE",EDGE,{"disambiguationData":[OSD([sQuery(id+"F0.wireOp",EDGE,"E0.bottom")])],"isStart":false})}),1.0]])]});
            cPlane(context, id + "F13", {"entities" : qUnion([Q0]), "cplaneType" : CPlaneType.OFFSET, "offset" : 100 * mm, "width" : 150 * mm, "height" : 150 * mm});
        }
        {
            var Q0;
            Q0=qCreatedBy(id+"F13.planeOp",FACE);
            var sketch = newSketch(context, id + "F14", { "sketchPlane" : qUnion([Q0])});
            skCircle(sketch, "E21", {"center": v(-190, 0) * mm, "radius": 15 * mm});
            skCircle(sketch, "E22", {"center": v(-130, 0) * mm, "radius": 15 * mm});
            skSolve(sketch);
        }
        {
            var Q0;
            Q0=makeQuery(id+"F14.imprint","IMPRINT",FACE,{"disambiguationData":[TD([[makeQuery(id+"F14.imprint","IMPRINT",EDGE,{"derivedFrom":sQuery(id+"F14.wireOp",EDGE,"E22")}),1.0]])]});
            var Q1;
            Q1=makeQuery(id+"F14.imprint","IMPRINT",FACE,{"disambiguationData":[TD([[makeQuery(id+"F14.imprint","IMPRINT",EDGE,{"derivedFrom":sQuery(id+"F14.wireOp",EDGE,"E21")}),1.0]])]});
            var Q2;
            Q2=makeQuery(id+"F1.opExtrude","SWEPT_BODY",BODY,{"disambiguationData":[OSD([sQuery(id+"F0.wireOp",EDGE,"E0.bottom"),sQuery(id+"F0.wireOp",EDGE,"E0.top"),sQuery(id+"F0.wireOp",EDGE,"E0.left"),sQuery(id+"F0.wireOp",EDGE,"E0.right")])]});
            extrude(context, id + "F15", {"entities" : qUnion([Q0, Q1]), "operationType" : NewBodyOperationType.ADD, "endBound" : BoundingType.UP_TO_BODY, "oppositeDirection" : true, "endBoundEntityBody" : qUnion([Q2]), "depth" : 25 * mm});
        }
        {
            var Q0;
            Q0=makeQuery(id+"F11.opExtrude","CAP_FACE",FACE,{"disambiguationData":[OSD([sQuery(id+"F10.wireOp",EDGE,"E20.0.52.0"),sQuery(id+"F10.wireOp",EDGE,"E20.3.52.0"),sQuery(id+"F10.wireOp",EDGE,"E20.6.52.0"),sQuery(id+"F10.wireOp",EDGE,"E20.9.52.0")])],"isStart":false});
            var sketch = newSketch(context, id + "F16", { "sketchPlane" : qUnion([Q0])});
            skLineSegment(sketch, "E23.bottom", {"start": v(229.07, 90) * mm, "end": v(-226.93, 90) * mm});
            skLineSegment(sketch, "E23.top", {"start": v(229.07, -30) * mm, "end": v(-226.93, -30) * mm});
            skLineSegment(sketch, "E23.left", {"start": v(229.07, 90) * mm, "end": v(229.07, -30) * mm});
            skLineSegment(sketch, "E23.right", {"start": v(-226.93, 90) * mm, "end": v(-226.93, -30) * mm});
            skSolve(sketch);
        }
        {
            var Q0;
            Q0=makeQuery(id+"F16.imprint","IMPRINT",FACE,{"disambiguationData":[TD([[makeQuery(id+"F16.imprint","IMPRINT",EDGE,{"derivedFrom":sQuery(id+"F16.wireOp",EDGE,"E23.bottom")}),1.0]])]});
            extrude(context, id + "F17", {"entities" : qUnion([Q0]), "operationType" : NewBodyOperationType.ADD, "depth" : 7 * mm});
        }
    });
